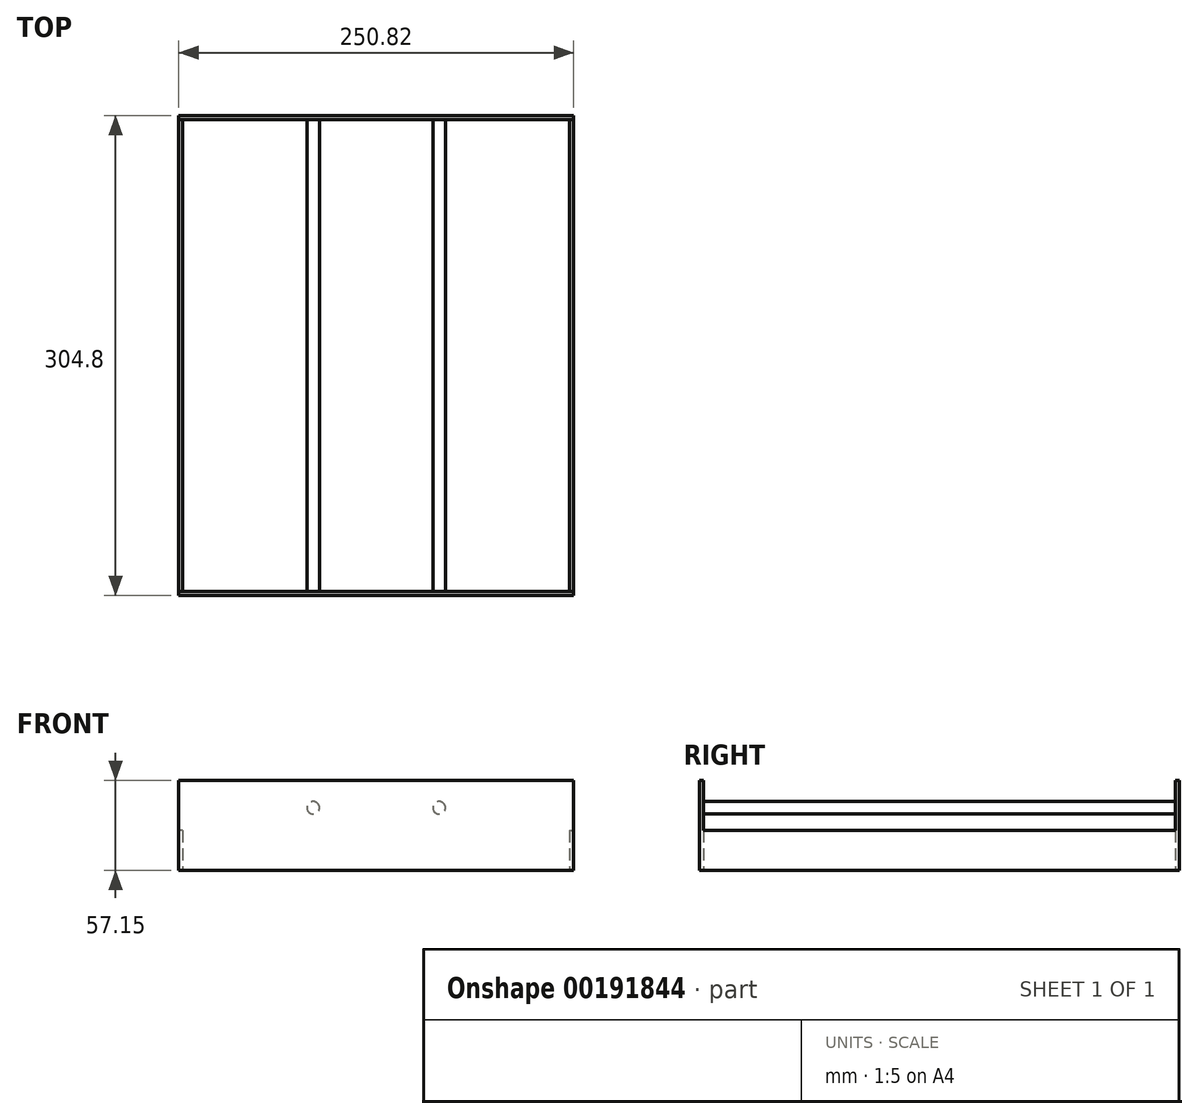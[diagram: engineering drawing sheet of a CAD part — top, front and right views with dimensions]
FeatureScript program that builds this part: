
annotation { "Feature Type Name" : "Feature", "Feature Type Description" : "" }
export const myFeature = defineFeature(function(context is Context, id is Id, definition is map)
    precondition{}
    {
        {
            var Q0;
            Q0=qCreatedBy(makeId("Top.planeOp"),FACE);
            var sketch = newSketch(context, id + "F0", { "sketchPlane" : qUnion([Q0])});
            skLineSegment(sketch, "E0", {"start": v(0, 0) * mm, "end": v(0, 304.8) * mm, "construction": true});
            skSolve(sketch);
        }
        {
            var Q0;
            Q0=qCreatedBy(makeId("Top.planeOp"),FACE);
            var sketch = newSketch(context, id + "F1", { "sketchPlane" : qUnion([Q0])});
            skLineSegment(sketch, "E1.bottom", {"start": v(125.41, 0) * mm, "end": v(-125.41, 0) * mm});
            skLineSegment(sketch, "E1.top", {"start": v(125.41, 2.54) * mm, "end": v(-125.41, 2.54) * mm});
            skLineSegment(sketch, "E1.left", {"start": v(125.41, 0) * mm, "end": v(125.41, 2.54) * mm});
            skLineSegment(sketch, "E1.right", {"start": v(-125.41, 0) * mm, "end": v(-125.41, 2.54) * mm});
            skPoint(sketch, "E1.middle", {"position": v(0, 1.27) * mm});
            skLineSegment(sketch, "E2.bottom", {"start": v(125.41, 302.26) * mm, "end": v(-125.41, 302.26) * mm});
            skLineSegment(sketch, "E2.top", {"start": v(125.41, 304.8) * mm, "end": v(-125.41, 304.8) * mm});
            skLineSegment(sketch, "E2.left", {"start": v(125.41, 302.26) * mm, "end": v(125.41, 304.8) * mm});
            skLineSegment(sketch, "E2.right", {"start": v(-125.41, 302.26) * mm, "end": v(-125.41, 304.8) * mm});
            skPoint(sketch, "E2.middle", {"position": v(0, 303.53) * mm});
            skSolve(sketch);
        }
        {
            var Q0;
            Q0 = qSketchRegion(id + "F1", true);
            extrude(context, id + "F2", {"entities" : qUnion([Q0]), "depth" : 57.15 * mm});
        }
        {
            var Q0;
            Q0=qCreatedBy(makeId("Front.planeOp"),FACE);
            var sketch = newSketch(context, id + "F3", { "sketchPlane" : qUnion([Q0])});
            skLineSegment(sketch, "E3.bottom", {"start": v(125.41, 0) * mm, "end": v(122.87, 0) * mm});
            skLineSegment(sketch, "E3.top", {"start": v(125.41, 25.4) * mm, "end": v(122.87, 25.4) * mm});
            skLineSegment(sketch, "E3.left", {"start": v(125.41, 0) * mm, "end": v(125.41, 25.4) * mm});
            skLineSegment(sketch, "E3.right", {"start": v(122.87, 0) * mm, "end": v(122.87, 25.4) * mm});
            skSolve(sketch);
        }
        {
            var Q0;
            Q0=makeQuery(id+"F3.imprint","IMPRINT",FACE,{"disambiguationData":[TD([[makeQuery(id+"F3.imprint","IMPRINT",EDGE,{"derivedFrom":sQuery(id+"F3.wireOp",EDGE,"E3.bottom")}),-1.0]])]});
            var Q1;
            Q1=makeQuery(id+"F2.opExtrude","SWEPT_FACE",FACE,{"disambiguationData":[OSD([sQuery(id+"F1.wireOp",EDGE,"E2.bottom")])]});
            extrude(context, id + "F4", {"entities" : qUnion([Q0]), "endBound" : BoundingType.UP_TO_SURFACE, "oppositeDirection" : true, "endBoundEntityFace" : qUnion([Q1]), "depth" : 25.4 * mm});
        }
        {
            var Q0;
            Q0=makeQuery(id+"F4.opExtrude","SWEPT_BODY",BODY,{"disambiguationData":[OSD([sQuery(id+"F3.wireOp",EDGE,"E3.bottom"),sQuery(id+"F3.wireOp",EDGE,"E3.top"),sQuery(id+"F3.wireOp",EDGE,"E3.left"),sQuery(id+"F3.wireOp",EDGE,"E3.right")])]});
            var Q1;
            Q1=qCreatedBy(makeId("Right.planeOp"),FACE);
            mirror(context, id + "F5", {"entities" : qUnion([Q0]), "mirrorPlane" : qUnion([Q1])});
        }
        {
            var Q0;
            Q0=qCreatedBy(makeId("Front.planeOp"),FACE);
            var sketch = newSketch(context, id + "F6", { "sketchPlane" : qUnion([Q0])});
            skLineSegment(sketch, "E4.bottom", {"start": v(0, 39.75) * mm, "end": v(40, 39.75) * mm, "construction": true});
            skLineSegment(sketch, "E4.top", {"start": v(0, 57.15) * mm, "end": v(40, 57.15) * mm, "construction": true});
            skLineSegment(sketch, "E4.left", {"start": v(0, 39.75) * mm, "end": v(0, 57.15) * mm, "construction": true});
            skLineSegment(sketch, "E4.right", {"start": v(40, 39.75) * mm, "end": v(40, 57.15) * mm, "construction": true});
            skCircle(sketch, "E5", {"center": v(40, 39.75) * mm, "radius": 4 * mm});
            skSolve(sketch);
        }
        {
            var Q0;
            Q0=makeQuery(id+"F6.imprint","IMPRINT",FACE,{"disambiguationData":[TD([[makeQuery(id+"F6.imprint","IMPRINT",EDGE,{"derivedFrom":sQuery(id+"F6.wireOp",EDGE,"E5")}),1.0]])]});
            var Q1;
            Q1=makeQuery(id+"F2.opExtrude","SWEPT_FACE",FACE,{"disambiguationData":[OSD([sQuery(id+"F1.wireOp",EDGE,"E2.bottom")])]});
            extrude(context, id + "F7", {"entities" : qUnion([Q0]), "operationType" : NewBodyOperationType.ADD, "endBound" : BoundingType.UP_TO_SURFACE, "oppositeDirection" : true, "endBoundEntityFace" : qUnion([Q1]), "depth" : 25.4 * mm});
        }
        {
            var Q0;
            Q0=makeQuery(id+"F2.opExtrude","SWEPT_BODY",BODY,{"disambiguationData":[OSD([sQuery(id+"F1.wireOp",EDGE,"E1.bottom"),sQuery(id+"F1.wireOp",EDGE,"E1.top"),sQuery(id+"F1.wireOp",EDGE,"E1.left"),sQuery(id+"F1.wireOp",EDGE,"E1.right")])]});
            var Q1;
            Q1=qCreatedBy(makeId("Right.planeOp"),FACE);
            mirror(context, id + "F8", {"operationType" : NewBodyOperationType.ADD, "entities" : qUnion([Q0]), "mirrorPlane" : qUnion([Q1])});
        }
    });
